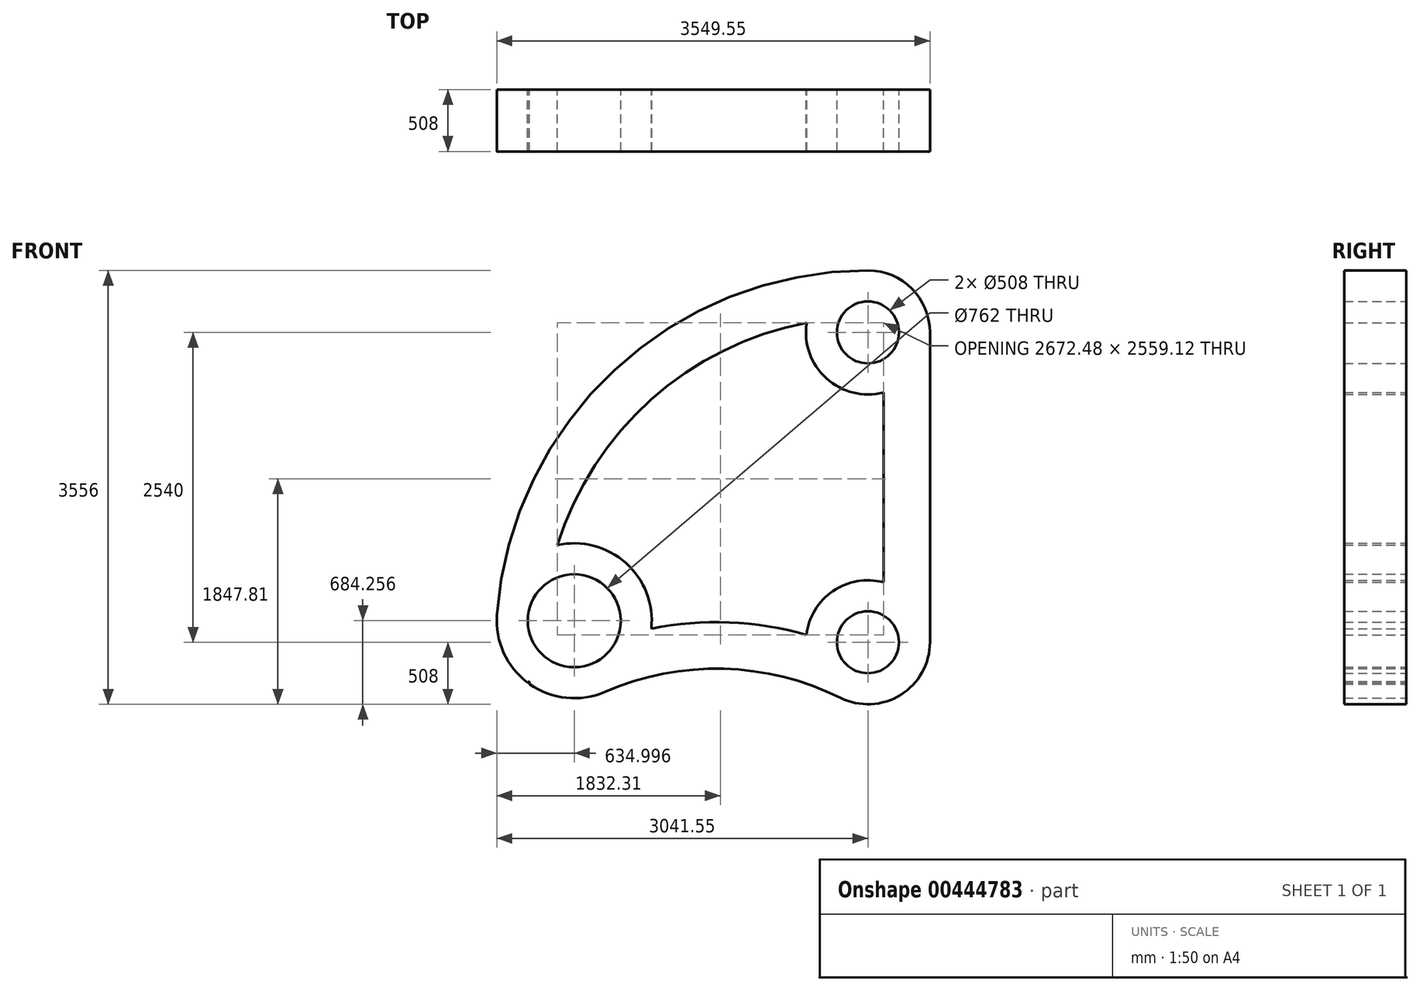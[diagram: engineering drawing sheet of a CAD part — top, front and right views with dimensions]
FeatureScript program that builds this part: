
annotation { "Feature Type Name" : "Feature", "Feature Type Description" : "" }
export const myFeature = defineFeature(function(context is Context, id is Id, definition is map)
    precondition{}
    {
        {
            var Q0;
            Q0=qCreatedBy(makeId("Front.planeOp"),FACE);
            var sketch = newSketch(context, id + "F0", { "sketchPlane" : qUnion([Q0])});
            skArc(sketch, "E0", {"start": v(-225.86, -455.03) * mm, "mid": v(267.7, -431.74) * mm, "end": v(508, 0) * mm});
            skCircle(sketch, "E1", {"center": v(0, 0) * mm, "radius": 254 * mm});
            skCircle(sketch, "E2", {"center": v(0, 2540) * mm, "radius": 254 * mm});
            skArc(sketch, "E3", {"start": v(508, 2540) * mm, "mid": v(359.21, 2899.21) * mm, "end": v(0, 3048) * mm});
            skLineSegment(sketch, "E4", {"start": v(508, 0) * mm, "end": v(508, 2540) * mm});
            skArc(sketch, "E5", {"start": v(0, 3048) * mm, "mid": v(-2075.05, 2232.59) * mm, "end": v(-3039.86, 222.64) * mm});
            skCircle(sketch, "E6", {"center": v(-2406.55, 176.26) * mm, "radius": 381 * mm});
            skArc(sketch, "E7", {"start": v(-3039.86, 222.64) * mm, "mid": v(-2773.94, -341.68) * mm, "end": v(-2153.44, -406.12) * mm});
            skArc(sketch, "E8.trimOffspring", {"start": v(-225.86, -455.03) * mm, "mid": v(-1184.24, -217.4) * mm, "end": v(-2153.44, -406.12) * mm});
            skArc(sketch, "E9.trimOffspring", {"start": v(-2775.56, -320.5) * mm, "mid": v(-2782.5, -325.4) * mm, "end": v(-2789.44, -330.33) * mm});
            skArc(sketch, "E10.trimOffspring", {"start": v(-2775.56, -320.5) * mm, "mid": v(-2774.27, -331.45) * mm, "end": v(-2772.94, -342.38) * mm});
            skArc(sketch, "E11.trimOffspring", {"start": v(-1774.96, 110.6) * mm, "mid": v(-1984.56, 650.75) * mm, "end": v(-2545.48, 795.87) * mm});
            skLineSegment(sketch, "E12.trimOffspring", {"start": v(-1738.33, 117.8) * mm, "end": v(-1773.97, 120.91) * mm});
            skArc(sketch, "E13.trimOffspring", {"start": v(-504.41, 60.25) * mm, "mid": v(-1136.64, 162.25) * mm, "end": v(-1774.96, 110.6) * mm});
            skPoint(sketch, "E14.orphan", {"position": v(0, -34.3) * mm});
            skLineSegment(sketch, "E15.trimOffspring", {"start": v(127, 491.87) * mm, "end": v(127, 2048.13) * mm});
            skArc(sketch, "E16.trimOffspring", {"start": v(127, 491.87) * mm, "mid": v(-286.68, 419.38) * mm, "end": v(-504.41, 60.25) * mm});
            skArc(sketch, "E17.trimOffspring", {"start": v(-501.76, 2619.38) * mm, "mid": v(-1775.59, 1990.02) * mm, "end": v(-2545.48, 795.87) * mm});
            skArc(sketch, "E18.trimOffspring", {"start": v(-501.76, 2619.38) * mm, "mid": v(-341.6, 2164) * mm, "end": v(127, 2048.13) * mm});
            skSolve(sketch);
        }
        {
            var Q0;
            Q0=makeQuery(id+"F0.imprint","IMPRINT",FACE,{"disambiguationData":[TD([[makeQuery(id+"F0.imprint","IMPRINT",EDGE,{"derivedFrom":sQuery(id+"F0.wireOp",EDGE,"E0")}),1.0]])]});
            extrude(context, id + "F1", {"entities" : qUnion([Q0]), "depth" : 508 * mm});
        }
    });
